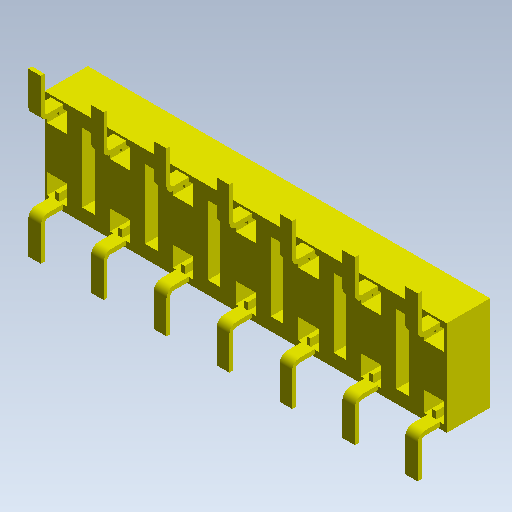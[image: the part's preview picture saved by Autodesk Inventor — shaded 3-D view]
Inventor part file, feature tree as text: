
AUTODESK INVENTOR PART (.ipt)
format: ipt  version: 2021 (Build 250183000, 183)  size: 400,384 bytes
history: native  units: mm (DEFAULTED — no unit token found)
features: other x7, extrude x4, sketch x4
ambient origin geometry x8: Origin, YZ Plane, XZ Plane, XY Plane, X Axis, Y Axis, Z Axis, Center Point
bodies: Solid1 (feature_tree)
feature tree (15):
  extrude  "Extrusion1"  Depth=16.256mm TaperAngle=0.0deg
  extrude  "Extrusion2"  Depth=10.16mm TaperAngle=0.0deg
  extrude  "Extrusion3"  [1 undecoded]
  extrude  "Extrusion4"  [1 undecoded]
  other  "pins_to_socket_XY"
  other  "pins_to_socket_YZ"
  other  "pins_to_socket_ZX"
  other  "pins_to_socket_X"
  other  "pins_to_socket_Y"
  other  "pins_to_socket_Z"
  other  "pins_to_socket_Center"
  sketch  "Sketch_11"  dims[d4=16.256mm d5=0.0mm d6=10.16mm d7=0.0mm]
  sketch  "Sketch_12"
  sketch  "Sketch_13"
  sketch  "Sketch_5"  dims[d0=1.7526mm d1=0.0mm d2=16.256mm d3=0.0mm]
note: 2 required parameter values undecoded (feature->parameter linkage not recoverable at this tier; creation-order binding heuristic only, values carry confidence <= 0.55)
